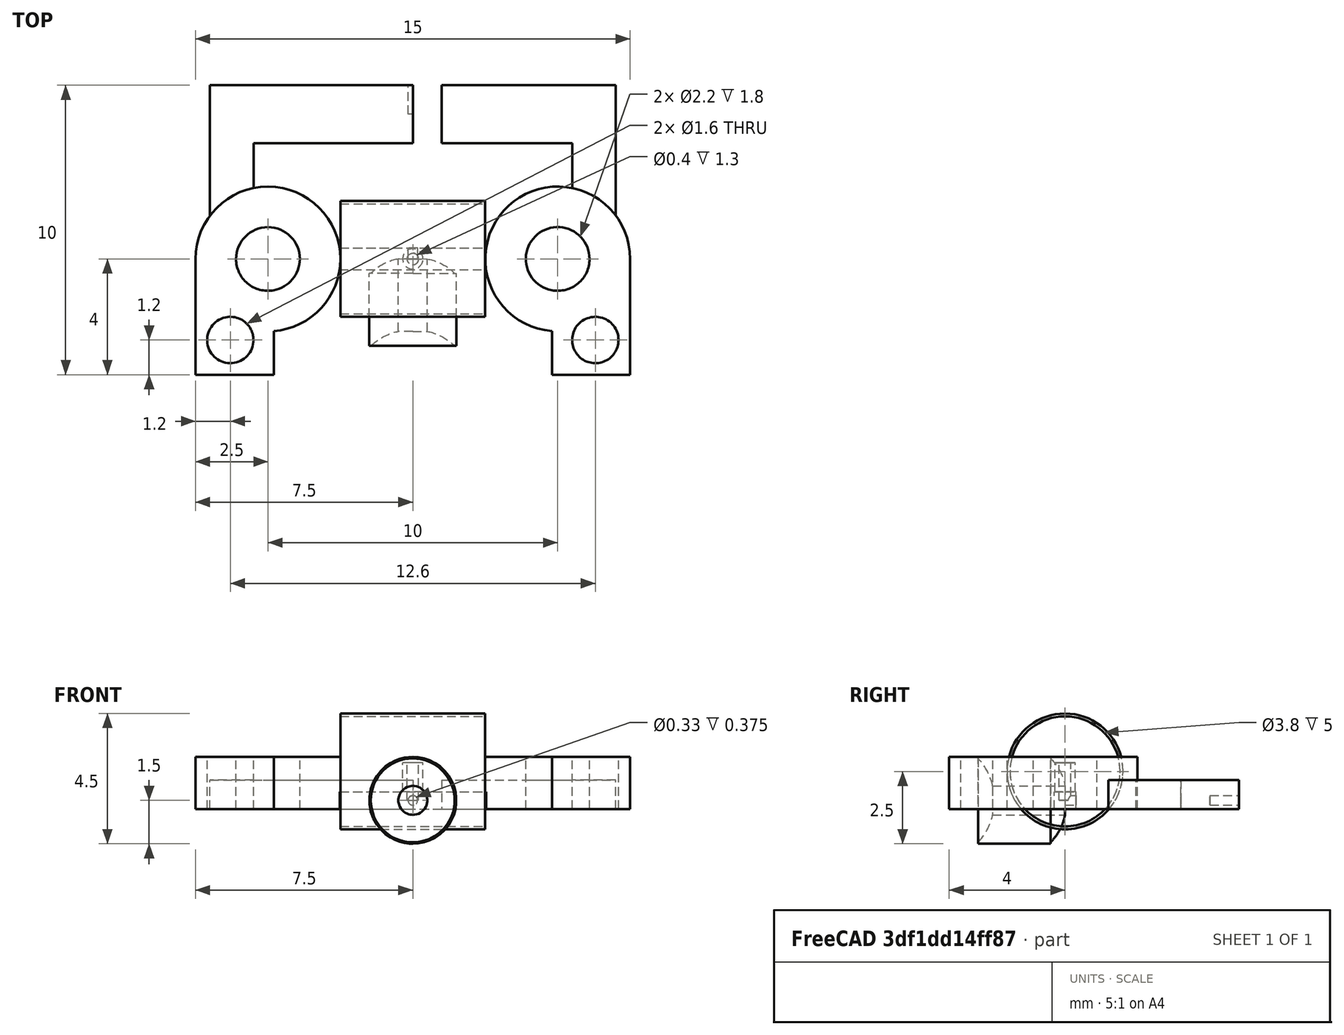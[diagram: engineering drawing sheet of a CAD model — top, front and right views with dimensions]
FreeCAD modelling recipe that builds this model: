
FCSTD DOCUMENT  (FreeCAD 0.18R16033 (Git))
Label: bowtie_prototype_1
License: All rights reserved
LicenseURL: http://en.wikipedia.org/wiki/All_rights_reserved
objects: Part::Cylinder×11, Part::Box×7, Part::MultiFuse×5, Part::Cut×4, Spreadsheet::Sheet×1, Part::Feature×1, App::Part×1
note: 28 computed .brp shape members not serialized (recipe doc carries the construction recipe); baked Part::Feature solids carry a one-line shape summary decoded from their .brp

FEATURE [Part::Cylinder] Cylinder138  label="BowTieInjectorWire"
  Angle = 360
  AttacherType = Attacher::AttachEngine3D
  Height = 8
  Placement = pos=(0,0,0) rot=(-1,0,0;1.5708rad)
  Radius = 0.165
  expr: Radius = 0.33 / 2
FEATURE [Part::Cylinder] Cylinder136  label="BowTieNozzle"
  Angle = 360
  AttacherType = Attacher::AttachEngine3D
  Height = 9
  Radius = 0.2
FEATURE [Part::Cylinder] Cylinder  label="MountingHole1"
  Angle = 360
  AttacherType = Attacher::AttachEngine3D
  Height = 4
  Placement = pos=(-5,0,-1) rot=(0,0,1;0rad)
  Radius = 1.1
  expr: Placement.Base.x = -Sizes.STRIP_LENGTH / 2
  expr: Radius = Sizes.MOUNTING_ID / 2
FEATURE [Part::Box] Box  label="Strip"
  AttacherType = Attacher::AttachEngine3D
  Height = 0.6
  Length = 10
  Placement = pos=(-5,-0.375,-0.3) rot=(0,0,1;0rad)
  Width = 0.75
  expr: Width = Sizes.STRIP_WIDTH
  expr: Placement.Base.y = -Sizes.STRIP_WIDTH / 2
  expr: Length = Sizes.STRIP_LENGTH
  expr: Placement.Base.x = -Sizes.STRIP_LENGTH / 2
  expr: Height = Sizes.STRIP_HEIGHT
  expr: Placement.Base.z = -Sizes.STRIP_HEIGHT / 2
FEATURE [Spreadsheet::Sheet] Spreadsheet  label="Sizes"
  cells = A1=Strip height; B1(STRIP_HEIGHT)=0.6; A2=Strip length; B2(STRIP_LENGTH)=10; A3=strip width; B3(STRIP_WIDTH)=0.75; A4=Injection width; B4(INJECTION_WIDTH)=1.5; A5=Injection length; B5(INJECTION_LENGTH)=1.5; A6=Mounting hole ID; B6(MOUNTING_ID)=2.2; A7=Nozzle ID; B7(NOZZLE_ID)=0.4; A8=Nozzle OD; B8(NOZZLE_OD)=0.7; A9=Mounting hole OD; B9(MOUNTING_OD)=5; A10=Nozzle height; B10(NOZZLE_HEIGHT)=1; A11=Mounting hole height; B11(MOUNTING_HEIGHT)=1.8
FEATURE [Part::Cylinder] Cylinder139  label="MountingHole2"
  Angle = 360
  AttacherType = Attacher::AttachEngine3D
  Height = 4
  Placement = pos=(5,0,-1) rot=(0,0,1;0rad)
  Radius = 1.1
  expr: Placement.Base.x = Sizes.STRIP_LENGTH / 2
  expr: Radius = Sizes.MOUNTING_ID / 2
FEATURE [Part::Cylinder] Cylinder140  label="Nozzle_OD"
  Angle = 360
  AttacherType = Attacher::AttachEngine3D
  Height = 1
  Placement = pos=(0,0,0.3) rot=(0,0,1;0rad)
  Radius = 0.35
  expr: Placement.Base.z = Sizes.STRIP_HEIGHT / 2
  expr: Height = Sizes.NOZZLE_HEIGHT
  expr: Radius = Sizes.NOZZLE_OD / 2
FEATURE [Part::Cylinder] Cylinder141  label="MountingHoleOD"
  Angle = 360
  AttacherType = Attacher::AttachEngine3D
  Height = 1.8
  Placement = pos=(-5,0,-0.3) rot=(0,0,1;0rad)
  Radius = 2.5
  expr: Radius = Sizes.MOUNTING_OD / 2
  expr: Placement.Base.z = -Sizes.STRIP_HEIGHT / 2
  expr: Height = Sizes.MOUNTING_HEIGHT
  expr: Placement.Base.x = -Sizes.STRIP_LENGTH / 2
FEATURE [Part::Cylinder] Cylinder142  label="MountingHoleOD001"
  Angle = 360
  AttacherType = Attacher::AttachEngine3D
  Height = 1.8
  Placement = pos=(5,0,-0.3) rot=(0,0,1;0rad)
  Radius = 2.5
  expr: Placement.Base.z = -Sizes.STRIP_HEIGHT / 2
  expr: Height = Sizes.MOUNTING_HEIGHT
  expr: Placement.Base.x = Sizes.STRIP_LENGTH / 2
  expr: Radius = Sizes.MOUNTING_OD / 2
FEATURE [Part::MultiFuse] Fusion
  Shapes = -> [Box,Cylinder142,Cylinder141,Cylinder140]
FEATURE [Part::MultiFuse] Fusion001
  Shapes = -> [Cylinder138,Cylinder136,Cylinder,Cylinder139]
FEATURE [Part::Feature] Part__Feature  label="1"
  shape: bbox 5.8 x 3 x 3.036 mm, 8 faces (baked)
FEATURE [App::Part] CER_4  label="CER-4"
  Group = -> [Part__Feature]
  Origin = -> Origin
  Placement = pos=(-5,0,0) rot=(1,0,0;1.5708rad)
FEATURE [Part::Box] Box001  label="Support"
  AttacherType = Attacher::AttachEngine3D
  Height = 1
  Length = 14
  Placement = pos=(-7,0,-0.3) rot=(0,0,1;0rad)
  Width = 6
FEATURE [Part::Box] Box002  label="SupportSubtract"
  AttacherType = Attacher::AttachEngine3D
  Height = 1
  Length = 11
  Placement = pos=(-5.5,0,-0.3) rot=(0,0,1;0rad)
  Width = 4
FEATURE [Part::Cut] Cut  label="Support001"
  Base = -> Box001
  Tool = -> Box002
FEATURE [Part::Box] Box003  label="Cube"
  AttacherType = Attacher::AttachEngine3D
  Height = 1.8
  Length = 2.7
  Placement = pos=(4.8,-4,-0.3) rot=(0,0,1;0rad)
  Width = 4
FEATURE [Part::Box] Box004  label="Cube001"
  AttacherType = Attacher::AttachEngine3D
  Height = 1.8
  Length = 2.7
  Placement = pos=(-7.5,-4,-0.3) rot=(0,0,1;0rad)
  Width = 4
FEATURE [Part::Cylinder] Cylinder143  label="Cylinder"
  Angle = 360
  AttacherType = Attacher::AttachEngine3D
  Height = 10
  Placement = pos=(-6.3,-2.8,-1) rot=(0,0,1;0rad)
  Radius = 0.8
  expr: Radius = 1.6 / 2
FEATURE [Part::Cylinder] Cylinder144  label="Cylinder001"
  Angle = 360
  AttacherType = Attacher::AttachEngine3D
  Height = 10
  Placement = pos=(6.3,-2.8,-1) rot=(0,0,1;0rad)
  Radius = 0.8
  expr: Radius = 1.6 / 2
FEATURE [Part::MultiFuse] Fusion002
  Shapes = -> [Cut,Box003,Box004,Fusion]
FEATURE [Part::MultiFuse] Fusion003
  Shapes = -> [Cylinder143,Cylinder144,Fusion001]
FEATURE [Part::Cut] Cut001
  Base = -> Fusion002
  Tool = -> Fusion003
FEATURE [Part::Box] Box005  label="Cube002"
  AttacherType = Attacher::AttachEngine3D
  Height = 1
  Length = 9
  Placement = pos=(-5,4,-0.3) rot=(0,0,1;0rad)
  Width = 1
FEATURE [Part::MultiFuse] Fusion004
  Shapes = -> [Cut001,Box005]
FEATURE [Part::Box] Box006  label="Cube003"
  AttacherType = Attacher::AttachEngine3D
  Height = 4
  Length = 1
  Placement = pos=(0,3,-1) rot=(0,0,1;0rad)
  Width = 6
FEATURE [Part::Cut] Cut002
  Base = -> Fusion004
  Tool = -> Box006
FEATURE [Part::Cylinder] Cylinder145  label="Cylinder002"
  Angle = 360
  AttacherType = Attacher::AttachEngine3D
  Height = 5
  Placement = pos=(-2.5,0,1) rot=(0,1,0;1.5708rad)
  Radius = 2
FEATURE [Part::Cylinder] Cylinder146  label="Cylinder003"
  Angle = 360
  AttacherType = Attacher::AttachEngine3D
  Height = 5
  Placement = pos=(-2.5,0,1) rot=(0,1,0;1.5708rad)
  Radius = 1.9
FEATURE [Part::Cut] Cut003
  Base = -> Cylinder145
  Tool = -> Cylinder146
